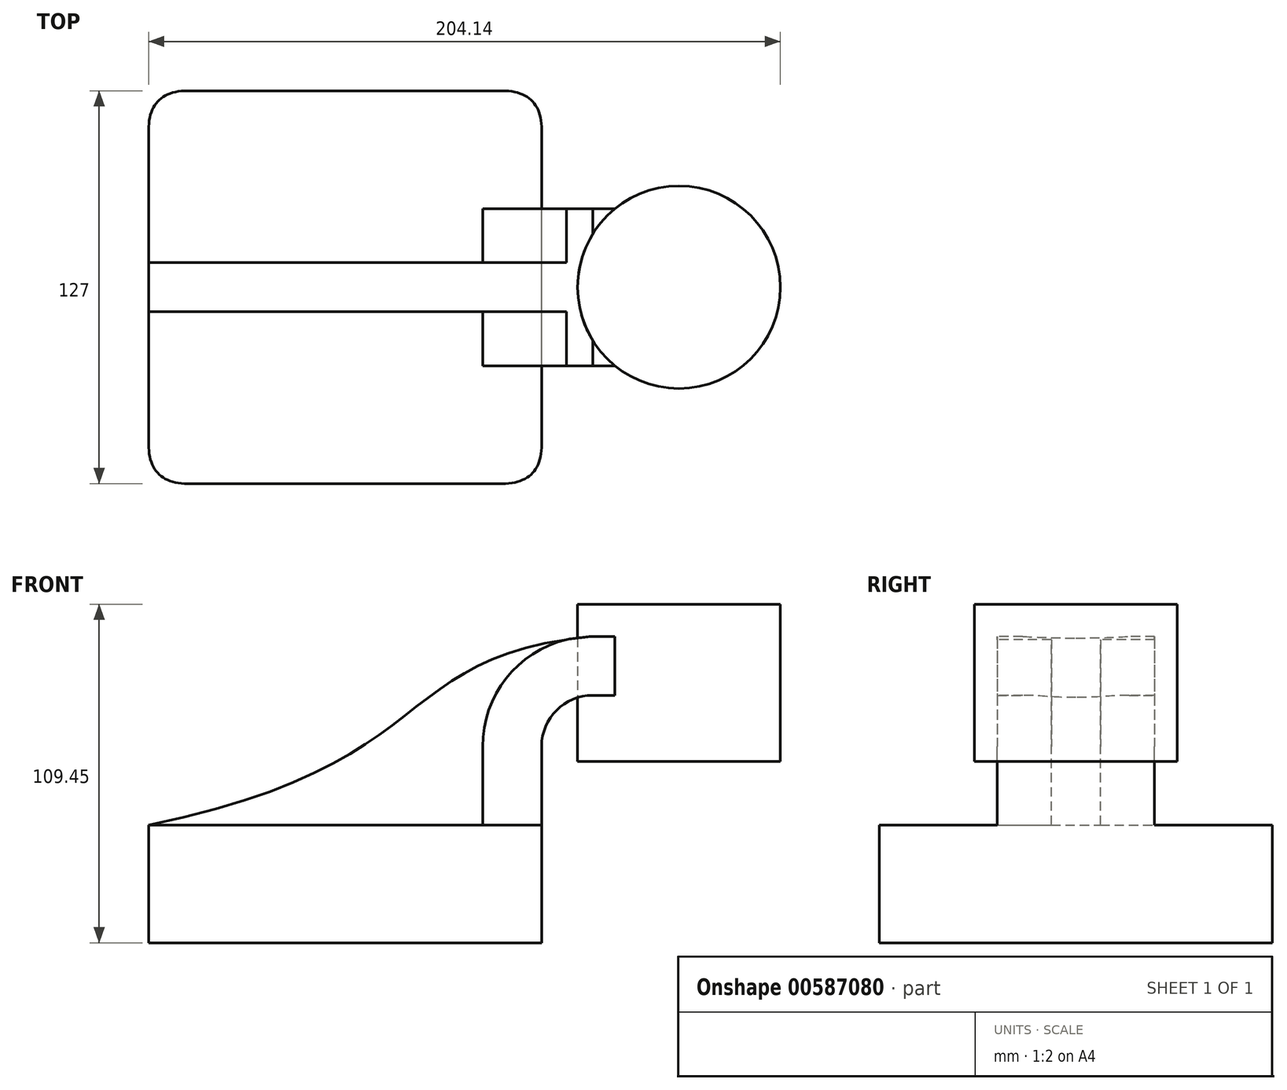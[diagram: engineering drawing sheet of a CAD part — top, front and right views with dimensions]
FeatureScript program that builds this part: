
annotation { "Feature Type Name" : "Feature", "Feature Type Description" : "" }
export const myFeature = defineFeature(function(context is Context, id is Id, definition is map)
    precondition{}
    {
        {
            var Q0;
            Q0=qCreatedBy(makeId("Front.planeOp"),FACE);
            var sketch = newSketch(context, id + "F0", { "sketchPlane" : qUnion([Q0])});
            skLineSegment(sketch, "E0.bottom", {"start": v(-63.5, 19.05) * mm, "end": v(63.5, 19.05) * mm});
            skLineSegment(sketch, "E0.top", {"start": v(-63.5, -19.05) * mm, "end": v(63.5, -19.05) * mm});
            skLineSegment(sketch, "E0.left", {"start": v(-63.5, 19.05) * mm, "end": v(-63.5, -19.05) * mm});
            skLineSegment(sketch, "E0.right", {"start": v(63.5, 19.05) * mm, "end": v(63.5, -19.05) * mm});
            skPoint(sketch, "E0.middle", {"position": v(0, 0) * mm});
            skLineSegment(sketch, "E1.bottom", {"start": v(89.84, 39.6) * mm, "end": v(140.64, 39.6) * mm});
            skLineSegment(sketch, "E1.top", {"start": v(89.84, 90.4) * mm, "end": v(140.64, 90.4) * mm});
            skLineSegment(sketch, "E1.left", {"start": v(89.84, 39.6) * mm, "end": v(89.84, 90.4) * mm});
            skLineSegment(sketch, "E1.right", {"start": v(140.64, 39.6) * mm, "end": v(140.64, 90.4) * mm});
            skPoint(sketch, "E1.middle", {"position": v(115.24, 65) * mm});
            skLineSegment(sketch, "E2", {"start": v(63.5, 19.05) * mm, "end": v(63.5, 44.45) * mm});
            skArc(sketch, "E3", {"start": v(63.5, 44.45) * mm, "mid": v(68.34, 56.12) * mm, "end": v(80, 60.96) * mm});
            skLineSegment(sketch, "E4", {"start": v(80, 60.96) * mm, "end": v(107.89, 60.96) * mm});
            skLineSegment(sketch, "E5.0", {"start": v(80, 80) * mm, "end": v(107.89, 80) * mm});
            skArc(sketch, "E5.1", {"start": v(44.45, 44.45) * mm, "mid": v(54.87, 69.6) * mm, "end": v(80, 80) * mm});
            skLineSegment(sketch, "E5.2", {"start": v(44.45, 19.05) * mm, "end": v(44.45, 44.45) * mm});
            skLineSegment(sketch, "E6", {"start": v(107.89, 39.6) * mm, "end": v(107.89, 90.4) * mm});
            skFitSpline(sketch, "E7", {"points": [v(-63.5, 19.05) * mm, v(80, 80) * mm], "startDerivative": vector(288.26, 58.38) * mm, "endDerivative": vector(198.95, 18.9) * mm});
            skSolve(sketch);
        }
        {
            var Q0;
            Q0=makeQuery(id+"F0.imprint","IMPRINT",FACE,{"disambiguationData":[TD([[makeQuery(id+"F0.imprint","IMPRINT",EDGE,{"derivedFrom":sQuery(id+"F0.wireOp",EDGE,"E0.top")}),1.0]])]});
            extrude(context, id + "F1", {"entities" : qUnion([Q0]), "endBound" : BoundingType.SYMMETRIC, "depth" : 127 * mm, "offsetDistance" : 25.4 * mm});
        }
        {
            var Q0;
            {var subQ1=sQuery(id+"F0.wireOp",EDGE,"E2");Q0=makeQuery(id+"F0.imprint","IMPRINT",FACE,{"disambiguationData":[TD([[makeQuery(id+"F0.imprint","IMPRINT",EDGE,{"derivedFrom":subQ1}),1.0]])]});}
            extrude(context, id + "F2", {"entities" : qUnion([Q0]), "operationType" : NewBodyOperationType.ADD, "endBound" : BoundingType.SYMMETRIC, "depth" : 50.8 * mm, "offsetDistance" : 25.4 * mm});
        }
        {
            var Q0;
            {var subQ3=sQuery(id+"F0.wireOp",EDGE,"E5.2");Q0=makeQuery(id+"F0.imprint","IMPRINT",FACE,{"disambiguationData":[TD([[makeQuery(id+"F0.imprint","IMPRINT",EDGE,{"derivedFrom":subQ3}),1.0]])]});}
            extrude(context, id + "F3", {"entities" : qUnion([Q0]), "operationType" : NewBodyOperationType.ADD, "endBound" : BoundingType.SYMMETRIC, "depth" : 15.88 * mm, "offsetDistance" : 25.4 * mm});
        }
        {
            var Q0;
            {var subQ4=sQuery(id+"F0.wireOp",EDGE,"E1.right");Q0=makeQuery(id+"F0.imprint","IMPRINT",FACE,{"disambiguationData":[TD([[makeQuery(id+"F0.imprint","IMPRINT",EDGE,{"derivedFrom":subQ4}),1.0]])]});}
            var Q1;
            Q1=sQuery(id+"F0.wireOp",EDGE,"E6");
            revolve(context, id + "F4", {"entities" : qUnion([Q0]), "axis" : qUnion([Q1]), "revolveType" : RevolveType.FULL});
        }
        {
            var Q0;
            Q0=makeQuery(id+"F1.opExtrude","CAP_EDGE",EDGE,{"disambiguationData":[OSD([sQuery(id+"F0.wireOp",EDGE,"E0.left")])],"isStart":false});
            var Q1;
            Q1=makeQuery(id+"F1.opExtrude","CAP_EDGE",EDGE,{"disambiguationData":[OSD([sQuery(id+"F0.wireOp",EDGE,"E0.right")])],"isStart":false});
            var Q2;
            Q2=makeQuery(id+"F1.opExtrude","CAP_EDGE",EDGE,{"disambiguationData":[OSD([sQuery(id+"F0.wireOp",EDGE,"E0.right")])],"isStart":true});
            var Q3;
            Q3=makeQuery(id+"F1.opExtrude","CAP_EDGE",EDGE,{"disambiguationData":[OSD([sQuery(id+"F0.wireOp",EDGE,"E0.left")])],"isStart":true});
            fillet(context, id + "F5", {"entities" : qUnion([Q0, Q1, Q2, Q3]), "radius" : 12.7 * mm, "tangentPropagation" : true, "rho" : 0.5, "crossSection" : FilletCrossSection.CONIC, "allowEdgeOverflow" : false});
        }
    });
